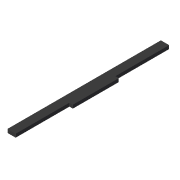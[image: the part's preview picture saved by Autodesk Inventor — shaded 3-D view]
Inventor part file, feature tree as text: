
AUTODESK INVENTOR PART (.ipt)
format: ipt  version: 2020 (Build 240168000, 168)  size: 87,552 bytes
history: native  units: mm
features: extrude x1, sketch x1
ambient origin geometry x8: Origin, YZ Plane, XZ Plane, XY Plane, X Axis, Y Axis, Z Axis, Center Point
bodies: Solid1 (feature_tree)
feature tree (2):
  extrude  "Extrusion1"  Depth=3.0mm
  sketch  "Sketch1"  dims[d0=134.0mm d1=3.0mm d2=40.0mm d3=7.0mm d4=3.0mm d5=0.0mm]
